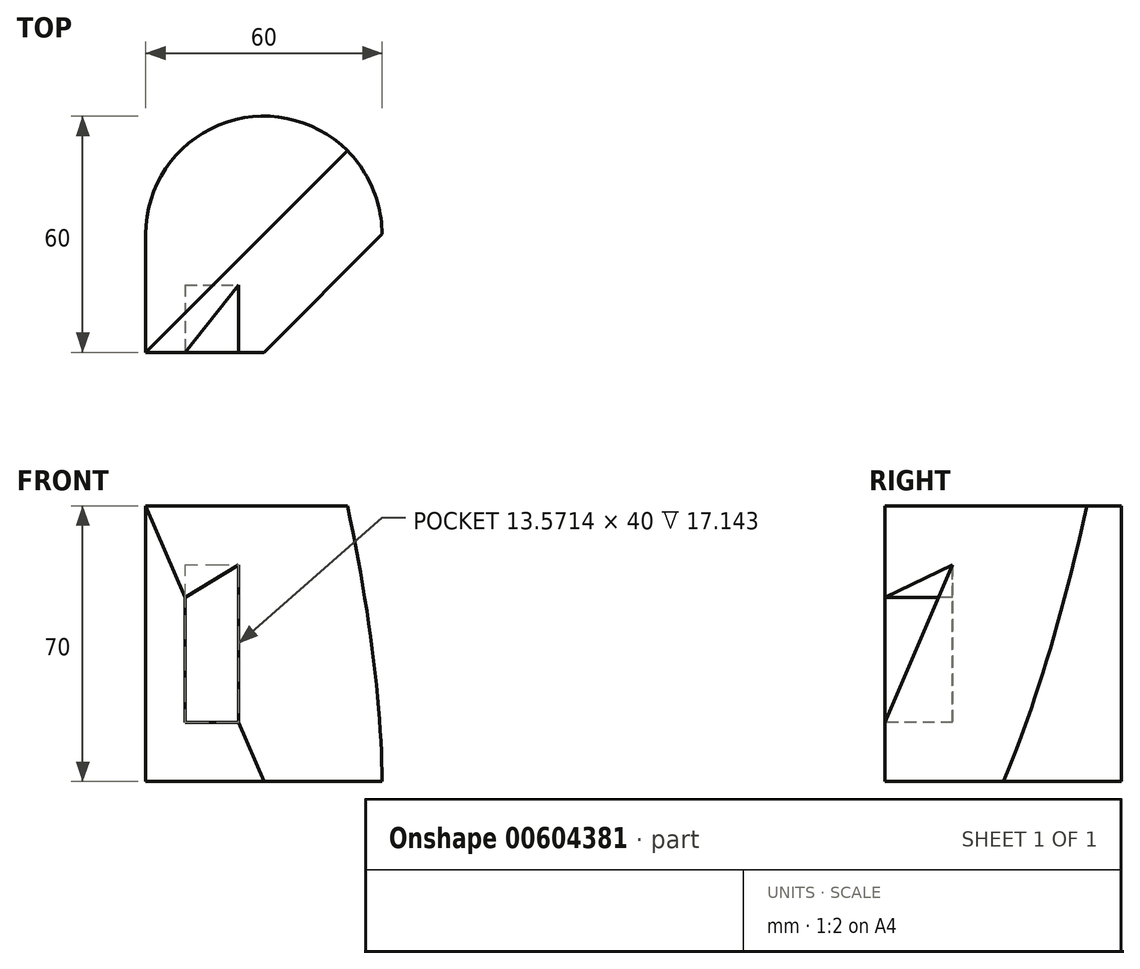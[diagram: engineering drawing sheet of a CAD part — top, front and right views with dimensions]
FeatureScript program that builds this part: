
annotation { "Feature Type Name" : "Feature", "Feature Type Description" : "" }
export const myFeature = defineFeature(function(context is Context, id is Id, definition is map)
    precondition{}
    {
        {
            var Q0;
            Q0=qCreatedBy(makeId("Top.planeOp"),FACE);
            var sketch = newSketch(context, id + "F0", { "sketchPlane" : qUnion([Q0])});
            skLineSegment(sketch, "E0", {"start": v(-30, -30) * mm, "end": v(-30, 0) * mm});
            skArc(sketch, "E1", {"start": v(30, 0) * mm, "mid": v(0, 30) * mm, "end": v(-30, 0) * mm});
            skLineSegment(sketch, "E2", {"start": v(30, 0) * mm, "end": v(0, -30) * mm});
            skLineSegment(sketch, "E3", {"start": v(0, -30) * mm, "end": v(-30, -30) * mm});
            skSolve(sketch);
        }
        {
            var Q0;
            Q0 = qSketchRegion(id + "F0", true);
            extrude(context, id + "F1", {"entities" : qUnion([Q0]), "depth" : 70 * mm, "offsetDistance" : 25 * mm});
        }
        {
            var Q0;
            Q0=makeQuery(id+"F1.opExtrude","SWEPT_FACE",FACE,{"disambiguationData":[OSD([sQuery(id+"F0.wireOp",EDGE,"E3")])]});
            var sketch = newSketch(context, id + "F2", { "sketchPlane" : qUnion([Q0])});
            skLineSegment(sketch, "E4", {"start": v(-30, 70) * mm, "end": v(0, 0) * mm});
            skSolve(sketch);
        }
        {
            var Q0;
            Q0=makeQuery(id+"F1.opExtrude","CAP_FACE",FACE,{"disambiguationData":[OSD([sQuery(id+"F0.wireOp",EDGE,"E0"),sQuery(id+"F0.wireOp",EDGE,"E1"),sQuery(id+"F0.wireOp",EDGE,"E2"),sQuery(id+"F0.wireOp",EDGE,"E3")])],"isStart":false});
            var sketch = newSketch(context, id + "F3", { "sketchPlane" : qUnion([Q0])});
            skLineSegment(sketch, "E5", {"start": v(-30, -30) * mm, "end": v(0, 0) * mm});
            skLineSegment(sketch, "E6", {"start": v(0, 0) * mm, "end": v(21.21, 21.21) * mm});
            skSolve(sketch);
        }
        {
            var Q0;
            Q0=makeQuery(id+"F2.imprint","IMPRINT",FACE,{"disambiguationData":[TD([[makeQuery(id+"F2.imprint","IMPRINT",EDGE,{"derivedFrom":sQuery(id+"F2.wireOp",EDGE,"E4")}),1.0]])]});
            var Q1;
            Q1=sQuery(id+"F3.wireOp",EDGE,"E5");
            var Q2;
            Q2=sQuery(id+"F3.wireOp",EDGE,"E6");
            sweep(context, id + "F4", {"operationType" : NewBodyOperationType.REMOVE, "profiles" : qUnion([Q0]), "path" : qUnion([Q1, Q2])});
        }
        {
            var Q0;
            Q0=makeQuery(id+"F1.opExtrude","SWEPT_FACE",FACE,{"disambiguationData":[OSD([sQuery(id+"F0.wireOp",EDGE,"E3")])]});
            var sketch = newSketch(context, id + "F5", { "sketchPlane" : qUnion([Q0])});
            skLineSegment(sketch, "E7", {"start": v(-20, 15) * mm, "end": v(-20, 46.67) * mm});
            skLineSegment(sketch, "E8", {"start": v(-20, 46.67) * mm, "end": v(-6.43, 55) * mm});
            skLineSegment(sketch, "E9", {"start": v(-6.43, 55) * mm, "end": v(-6.43, 15) * mm});
            skLineSegment(sketch, "E10", {"start": v(-6.43, 15) * mm, "end": v(-20, 15) * mm});
            skSolve(sketch);
        }
        {
            var Q0;
            Q0 = qSketchRegion(id + "F5", true);
            extrude(context, id + "F6", {"entities" : qUnion([Q0]), "operationType" : NewBodyOperationType.REMOVE, "oppositeDirection" : true, "depth" : 25 * mm, "offsetDistance" : 25 * mm});
        }
        {
            var Q0;
            Q0=makeQuery(id+"F6.boolean.opBoolean","COPY",FACE,{"derivedFrom":makeQuery(id+"F6.opExtrude","CAP_FACE",FACE,{"disambiguationData":[OSD([sQuery(id+"F5.wireOp",EDGE,"E7"),sQuery(id+"F5.wireOp",EDGE,"E8"),sQuery(id+"F5.wireOp",EDGE,"E9"),sQuery(id+"F5.wireOp",EDGE,"E10")])],"isStart":false})});
            var Q1;
            Q1=makeQuery(id+"F6.boolean.opBoolean","COPY",EDGE,{"derivedFrom":makeQuery(id+"F6.opExtrude","SWEPT_EDGE",EDGE,{"disambiguationData":[OSD([sQuery(id+"F5.wireOp",EDGE,"E8"),sQuery(id+"F5.wireOp",EDGE,"E9")])]})});
            sweep(context, id + "F7", {"operationType" : NewBodyOperationType.ADD, "profiles" : qUnion([Q0]), "path" : qUnion([Q1])});
        }
    });
